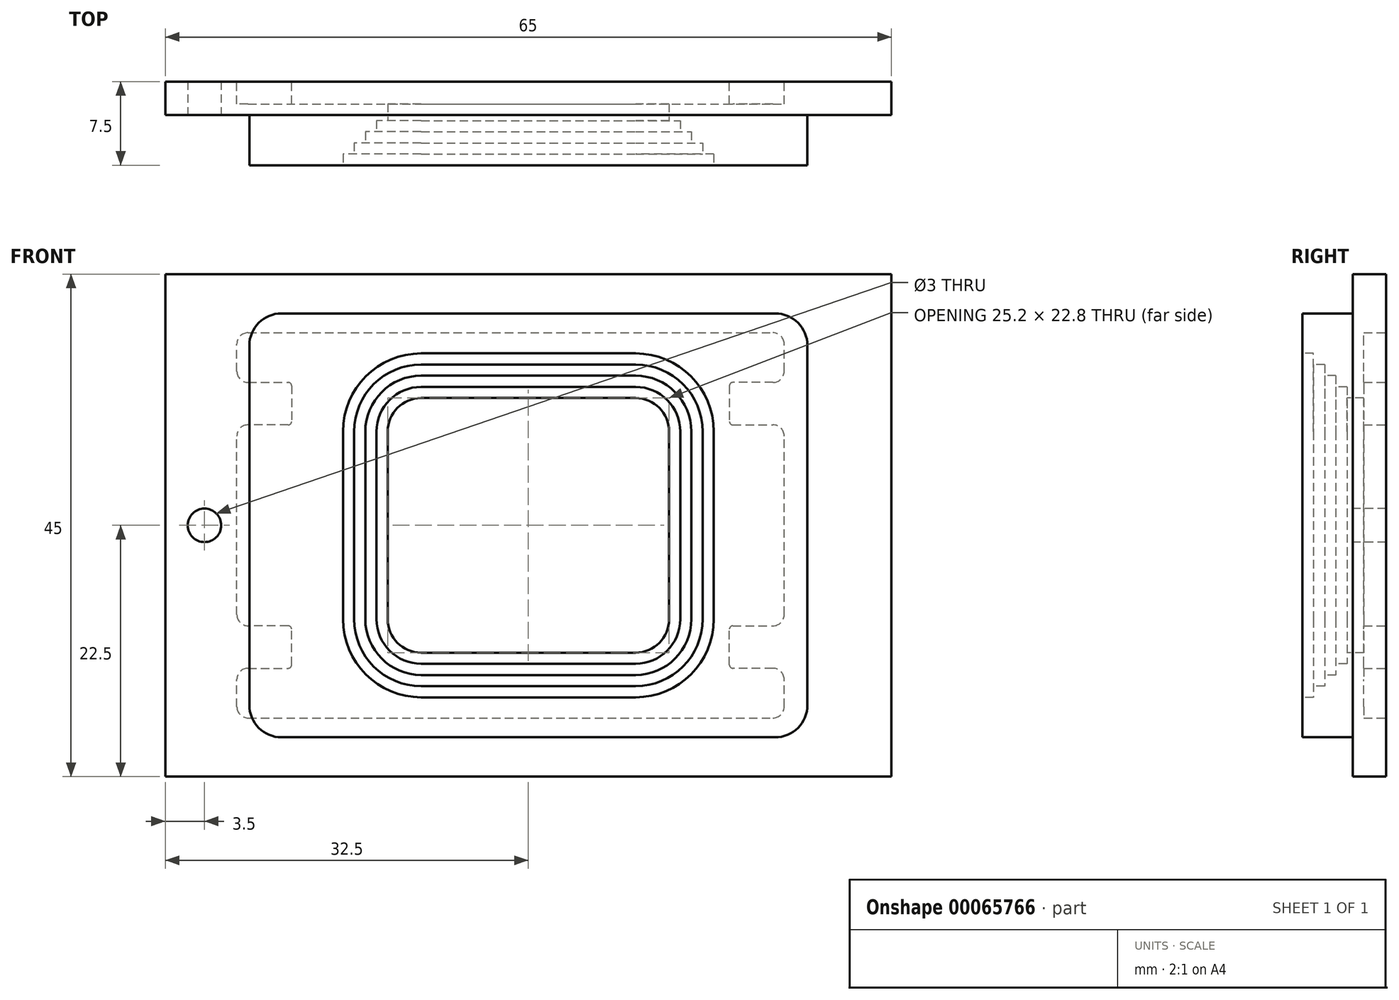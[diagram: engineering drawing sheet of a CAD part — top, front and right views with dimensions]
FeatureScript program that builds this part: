
annotation { "Feature Type Name" : "Feature", "Feature Type Description" : "" }
export const myFeature = defineFeature(function(context is Context, id is Id, definition is map)
    precondition{}
    {
        {
            var Q0;
            Q0=qCreatedBy(makeId("Front.planeOp"),FACE);
            var sketch = newSketch(context, id + "F0", { "sketchPlane" : qUnion([Q0])});
            skLineSegment(sketch, "E0.bottom", {"start": v(-32.5, 22.5) * mm, "end": v(32.5, 22.5) * mm});
            skLineSegment(sketch, "E0.top", {"start": v(-32.5, -22.5) * mm, "end": v(32.5, -22.5) * mm});
            skLineSegment(sketch, "E0.left", {"start": v(-32.5, 22.5) * mm, "end": v(-32.5, -22.5) * mm});
            skLineSegment(sketch, "E0.right", {"start": v(32.5, 22.5) * mm, "end": v(32.5, -22.5) * mm});
            skPoint(sketch, "E1.visualSharp", {"position": v(-32.5, 22.5) * mm});
            skLineSegment(sketch, "E1.filletArc", {"start": v(-32.5, 22.5) * mm, "end": v(-32.5, 22.5) * mm});
            skPoint(sketch, "E2.visualSharp", {"position": v(32.5, 22.5) * mm});
            skLineSegment(sketch, "E2.filletArc", {"start": v(32.5, 22.5) * mm, "end": v(32.5, 22.5) * mm});
            skPoint(sketch, "E3.visualSharp", {"position": v(32.5, -22.5) * mm});
            skLineSegment(sketch, "E3.filletArc", {"start": v(32.5, -22.5) * mm, "end": v(32.5, -22.5) * mm});
            skPoint(sketch, "E4.visualSharp", {"position": v(-32.5, -22.5) * mm});
            skLineSegment(sketch, "E4.filletArc", {"start": v(-32.5, -22.5) * mm, "end": v(-32.5, -22.5) * mm});
            skPoint(sketch, "E5", {"position": v(0, 22.5) * mm});
            skPoint(sketch, "E6", {"position": v(32.5, 0) * mm});
            skSolve(sketch);
        }
        {
            var Q0;
            Q0=makeQuery(id+"F0.imprint","IMPRINT",FACE,{"disambiguationData":[TD([[makeQuery(id+"F0.imprint","IMPRINT",EDGE,{"derivedFrom":sQuery(id+"F0.wireOp",EDGE,"E0.bottom")}),-1.0]])]});
            var Q1;
            Q1=makeQuery(id+"F0.imprint","IMPRINT",FACE,{"disambiguationData":[TD([[makeQuery(id+"F0.imprint","IMPRINT",EDGE,{"derivedFrom":sQuery(id+"F0.wireOp",EDGE,"E0.bottom")}),-1.0]])]});
            extrude(context, id + "F1", {"entities" : qUnion([Q0, Q1]), "depth" : 3 * mm});
        }
        {
            var Q0;
            Q0=makeQuery(id+"F1.opExtrude","CAP_FACE",FACE,{"disambiguationData":[OSD([sQuery(id+"F0.wireOp",EDGE,"E0.bottom"),sQuery(id+"F0.wireOp",EDGE,"E0.top"),sQuery(id+"F0.wireOp",EDGE,"E0.left"),sQuery(id+"F0.wireOp",EDGE,"E0.right"),sQuery(id+"F0.wireOp",EDGE,"E1.filletArc"),sQuery(id+"F0.wireOp",EDGE,"E2.filletArc"),sQuery(id+"F0.wireOp",EDGE,"E3.filletArc"),sQuery(id+"F0.wireOp",EDGE,"E4.filletArc")])],"isStart":false});
            var sketch = newSketch(context, id + "F2", { "sketchPlane" : qUnion([Q0])});
            skLineSegment(sketch, "E7.bottom", {"start": v(-22.09, 18.99) * mm, "end": v(22.09, 18.99) * mm});
            skLineSegment(sketch, "E7.top", {"start": v(-22.09, -18.99) * mm, "end": v(22.09, -18.99) * mm});
            skLineSegment(sketch, "E7.left", {"start": v(-24.98, 16.09) * mm, "end": v(-24.98, -16.09) * mm});
            skLineSegment(sketch, "E7.right", {"start": v(24.98, 16.09) * mm, "end": v(24.98, -16.09) * mm});
            skPoint(sketch, "E8", {"position": v(0, 18.99) * mm});
            skPoint(sketch, "E9", {"position": v(24.98, 0) * mm});
            skPoint(sketch, "E10.visualSharp", {"position": v(-24.98, 18.99) * mm});
            skArc(sketch, "E10.filletArc", {"start": v(-22.09, 18.99) * mm, "mid": v(-24.14, 18.14) * mm, "end": v(-24.98, 16.09) * mm});
            skPoint(sketch, "E11.visualSharp", {"position": v(24.99, -18.98) * mm});
            skArc(sketch, "E11.filletArc", {"start": v(22.09, -18.99) * mm, "mid": v(24.14, -18.14) * mm, "end": v(24.98, -16.09) * mm});
            skPoint(sketch, "E12.visualSharp", {"position": v(24.99, 18.98) * mm});
            skArc(sketch, "E12.filletArc", {"start": v(24.98, 16.09) * mm, "mid": v(24.14, 18.14) * mm, "end": v(22.09, 18.99) * mm});
            skPoint(sketch, "E13.visualSharp", {"position": v(-24.98, -18.99) * mm});
            skArc(sketch, "E13.filletArc", {"start": v(-24.98, -16.09) * mm, "mid": v(-24.14, -18.14) * mm, "end": v(-22.09, -18.99) * mm});
            skSolve(sketch);
        }
        {
            var Q0;
            Q0=makeQuery(id+"F2.imprint","IMPRINT",FACE,{"disambiguationData":[TD([[makeQuery(id+"F2.imprint","IMPRINT",EDGE,{"derivedFrom":sQuery(id+"F2.wireOp",EDGE,"E7.bottom")}),-1.0]])]});
            extrude(context, id + "F3", {"entities" : qUnion([Q0]), "operationType" : NewBodyOperationType.ADD, "depth" : 4.5 * mm});
        }
        {
            var Q0;
            Q0=makeQuery(id+"F3.opExtrude","CAP_FACE",FACE,{"disambiguationData":[OSD([sQuery(id+"F2.wireOp",EDGE,"E7.bottom"),sQuery(id+"F2.wireOp",EDGE,"E7.top"),sQuery(id+"F2.wireOp",EDGE,"E7.left"),sQuery(id+"F2.wireOp",EDGE,"E7.right"),sQuery(id+"F2.wireOp",EDGE,"E10.filletArc"),sQuery(id+"F2.wireOp",EDGE,"E11.filletArc"),sQuery(id+"F2.wireOp",EDGE,"E12.filletArc"),sQuery(id+"F2.wireOp",EDGE,"E13.filletArc")])],"isStart":false});
            var sketch = newSketch(context, id + "F4", { "sketchPlane" : qUnion([Q0])});
            skLineSegment(sketch, "E14.bottom", {"start": v(-9.6, 11.4) * mm, "end": v(9.6, 11.4) * mm});
            skLineSegment(sketch, "E14.top", {"start": v(-9.6, -11.4) * mm, "end": v(9.6, -11.4) * mm});
            skLineSegment(sketch, "E14.left", {"start": v(-12.6, 8.4) * mm, "end": v(-12.6, -8.4) * mm});
            skLineSegment(sketch, "E14.right", {"start": v(12.6, 8.4) * mm, "end": v(12.6, -8.4) * mm});
            skPoint(sketch, "E15", {"position": v(0, 11.4) * mm});
            skPoint(sketch, "E16", {"position": v(12.6, 0) * mm});
            skPoint(sketch, "E17.visualSharp", {"position": v(-12.6, 11.4) * mm});
            skArc(sketch, "E17.filletArc", {"start": v(-9.6, 11.4) * mm, "mid": v(-11.72, 10.52) * mm, "end": v(-12.6, 8.4) * mm});
            skPoint(sketch, "E18.visualSharp", {"position": v(12.6, 11.4) * mm});
            skArc(sketch, "E18.filletArc", {"start": v(12.6, 8.4) * mm, "mid": v(11.72, 10.52) * mm, "end": v(9.6, 11.4) * mm});
            skPoint(sketch, "E19.visualSharp", {"position": v(12.6, -11.4) * mm});
            skArc(sketch, "E19.filletArc", {"start": v(9.6, -11.4) * mm, "mid": v(11.72, -10.52) * mm, "end": v(12.6, -8.4) * mm});
            skPoint(sketch, "E20.visualSharp", {"position": v(-12.6, -11.4) * mm});
            skArc(sketch, "E20.filletArc", {"start": v(-12.6, -8.4) * mm, "mid": v(-11.72, -10.52) * mm, "end": v(-9.6, -11.4) * mm});
            skCircle(sketch, "E21", {"center": v(-29, 0) * mm, "radius": 1.5 * mm});
            skCircle(sketch, "E22.MirrorC", {"center": v(29, 0) * mm, "radius": 1.5 * mm});
            skSolve(sketch);
        }
        {
            var Q0;
            Q0=makeQuery(id+"F4.imprint","IMPRINT",FACE,{"disambiguationData":[TD([[makeQuery(id+"F4.imprint","IMPRINT",EDGE,{"derivedFrom":sQuery(id+"F4.wireOp",EDGE,"E14.bottom")}),-1.0]])]});
            var Q1;
            Q1=makeQuery(id+"F4.imprint","IMPRINT",FACE,{"disambiguationData":[TD([[makeQuery(id+"F4.imprint","IMPRINT",EDGE,{"derivedFrom":sQuery(id+"F4.wireOp",EDGE,"E21")}),1.0]])]});
            var Q2;
            Q2=makeQuery(id+"F4.imprint","IMPRINT",FACE,{"disambiguationData":[TD([[makeQuery(id+"F4.imprint","IMPRINT",EDGE,{"derivedFrom":sQuery(id+"F4.wireOp",EDGE,"E22.MirrorC")}),-1.0]])]});
            extrude(context, id + "F5", {"entities" : qUnion([Q0, Q1, Q2]), "operationType" : NewBodyOperationType.REMOVE, "oppositeDirection" : true, "depth" : 25 * mm});
        }
        {
            var Q0;
            Q0=makeQuery(id+"F1.opExtrude","CAP_FACE",FACE,{"disambiguationData":[OSD([sQuery(id+"F0.wireOp",EDGE,"E0.bottom"),sQuery(id+"F0.wireOp",EDGE,"E0.top"),sQuery(id+"F0.wireOp",EDGE,"E0.left"),sQuery(id+"F0.wireOp",EDGE,"E0.right")])],"isStart":true});
            var sketch = newSketch(context, id + "F6", { "sketchPlane" : qUnion([Q0])});
            skPoint(sketch, "E23", {"position": v(-32.5, 0) * mm});
            skPoint(sketch, "E23.positionSnap0", {"position": v(-22.9, 0) * mm});
            skLineSegment(sketch, "E24", {"start": v(-21.9, -12.8) * mm, "end": v(-18.3, -12.8) * mm});
            skLineSegment(sketch, "E25", {"start": v(-18, -12.5) * mm, "end": v(-18, -9.3) * mm});
            skLineSegment(sketch, "E26", {"start": v(-18.3, -9) * mm, "end": v(-21.9, -9) * mm});
            skLineSegment(sketch, "E27", {"start": v(-21.9, 12.8) * mm, "end": v(-18.3, 12.8) * mm});
            skLineSegment(sketch, "E28", {"start": v(-18, 12.5) * mm, "end": v(-18, 9.3) * mm});
            skLineSegment(sketch, "E29", {"start": v(-18.3, 9) * mm, "end": v(-21.9, 9) * mm});
            skLineSegment(sketch, "E30", {"start": v(1.6, 17.25) * mm, "end": v(1.6, -17.25) * mm, "construction": true});
            skLineSegment(sketch, "E31", {"start": v(-22.9, -16.25) * mm, "end": v(-22.9, -13.8) * mm});
            skLineSegment(sketch, "E32", {"start": v(-22.9, -8) * mm, "end": v(-22.9, 8) * mm});
            skLineSegment(sketch, "E33", {"start": v(-22.9, 13.8) * mm, "end": v(-22.9, 16.25) * mm});
            skPoint(sketch, "E34.visualSharp", {"position": v(-22.9, 12.8) * mm});
            skArc(sketch, "E34.filletArc", {"start": v(-22.9, 13.8) * mm, "mid": v(-22.6, 13.1) * mm, "end": v(-21.9, 12.8) * mm});
            skPoint(sketch, "E35.visualSharp", {"position": v(-22.9, 17.25) * mm});
            skArc(sketch, "E35.filletArc", {"start": v(-21.9, 17.25) * mm, "mid": v(-22.6, 16.96) * mm, "end": v(-22.9, 16.25) * mm});
            skPoint(sketch, "E36.visualSharp", {"position": v(-22.9, -9) * mm});
            skArc(sketch, "E36.filletArc", {"start": v(-22.9, -8) * mm, "mid": v(-22.6, -8.7) * mm, "end": v(-21.9, -9) * mm});
            skPoint(sketch, "E37.visualSharp", {"position": v(-22.9, -17.25) * mm});
            skArc(sketch, "E37.filletArc", {"start": v(-22.9, -16.25) * mm, "mid": v(-22.6, -16.96) * mm, "end": v(-21.9, -17.25) * mm});
            skPoint(sketch, "E38.visualSharp", {"position": v(-18, 9) * mm});
            skArc(sketch, "E38.filletArc", {"start": v(-18.3, 9) * mm, "mid": v(-18.09, 9.09) * mm, "end": v(-18, 9.3) * mm});
            skPoint(sketch, "E39.visualSharp", {"position": v(-18, 12.8) * mm});
            skArc(sketch, "E39.filletArc", {"start": v(-18, 12.5) * mm, "mid": v(-18.09, 12.71) * mm, "end": v(-18.3, 12.8) * mm});
            skPoint(sketch, "E40.visualSharp", {"position": v(-18, -9) * mm});
            skArc(sketch, "E40.filletArc", {"start": v(-18, -9.3) * mm, "mid": v(-18.09, -9.09) * mm, "end": v(-18.3, -9) * mm});
            skPoint(sketch, "E41.visualSharp", {"position": v(-18, -12.8) * mm});
            skArc(sketch, "E41.filletArc", {"start": v(-18.3, -12.8) * mm, "mid": v(-18.09, -12.71) * mm, "end": v(-18, -12.5) * mm});
            skPoint(sketch, "E42.visualSharp", {"position": v(-22.9, 9) * mm});
            skArc(sketch, "E42.filletArc", {"start": v(-21.9, 9) * mm, "mid": v(-22.6, 8.7) * mm, "end": v(-22.9, 8) * mm});
            skPoint(sketch, "E43.visualSharp", {"position": v(-22.9, -12.8) * mm});
            skArc(sketch, "E43.filletArc", {"start": v(-21.9, -12.8) * mm, "mid": v(-22.6, -13.1) * mm, "end": v(-22.9, -13.8) * mm});
            skArc(sketch, "E44.MirrorCS", {"start": v(26.1, -16.25) * mm, "mid": v(25.8, -16.96) * mm, "end": v(25.1, -17.25) * mm});
            skArc(sketch, "E45.MirrorCS", {"start": v(25.1, -12.8) * mm, "mid": v(25.8, -13.1) * mm, "end": v(26.1, -13.8) * mm});
            skLineSegment(sketch, "E46.MirrorCS", {"start": v(25.1, -12.8) * mm, "end": v(21.5, -12.8) * mm});
            skArc(sketch, "E47.MirrorCS", {"start": v(21.5, -12.8) * mm, "mid": v(21.29, -12.71) * mm, "end": v(21.2, -12.5) * mm});
            skLineSegment(sketch, "E48.MirrorCS", {"start": v(21.2, -12.5) * mm, "end": v(21.2, -9.3) * mm});
            skArc(sketch, "E49.MirrorCS", {"start": v(21.2, -9.3) * mm, "mid": v(21.29, -9.09) * mm, "end": v(21.5, -9) * mm});
            skLineSegment(sketch, "E50.MirrorCS", {"start": v(21.5, -9) * mm, "end": v(25.1, -9) * mm});
            skArc(sketch, "E51.MirrorCS", {"start": v(26.1, -8) * mm, "mid": v(25.8, -8.7) * mm, "end": v(25.1, -9) * mm});
            skLineSegment(sketch, "E52.MirrorCS", {"start": v(26.1, -8) * mm, "end": v(26.1, 8) * mm});
            skArc(sketch, "E53.MirrorCS", {"start": v(25.1, 9) * mm, "mid": v(25.8, 8.7) * mm, "end": v(26.1, 8) * mm});
            skLineSegment(sketch, "E54.MirrorCS", {"start": v(21.5, 9) * mm, "end": v(25.1, 9) * mm});
            skArc(sketch, "E55.MirrorCS", {"start": v(21.5, 9) * mm, "mid": v(21.29, 9.09) * mm, "end": v(21.2, 9.3) * mm});
            skLineSegment(sketch, "E56.MirrorCS", {"start": v(21.2, 12.5) * mm, "end": v(21.2, 9.3) * mm});
            skArc(sketch, "E57.MirrorCS", {"start": v(21.2, 12.5) * mm, "mid": v(21.29, 12.71) * mm, "end": v(21.5, 12.8) * mm});
            skLineSegment(sketch, "E58.MirrorCS", {"start": v(25.1, 12.8) * mm, "end": v(21.5, 12.8) * mm});
            skArc(sketch, "E59.MirrorCS", {"start": v(26.1, 13.8) * mm, "mid": v(25.8, 13.1) * mm, "end": v(25.1, 12.8) * mm});
            skLineSegment(sketch, "E60.MirrorCS", {"start": v(26.1, 13.8) * mm, "end": v(26.1, 16.25) * mm});
            skArc(sketch, "E61.MirrorCS", {"start": v(25.1, 17.25) * mm, "mid": v(25.8, 16.96) * mm, "end": v(26.1, 16.25) * mm});
            skLineSegment(sketch, "E62", {"start": v(25.1, -17.25) * mm, "end": v(-21.9, -17.25) * mm});
            skLineSegment(sketch, "E63", {"start": v(25.1, 17.25) * mm, "end": v(-21.9, 17.25) * mm});
            skLineSegment(sketch, "E64", {"start": v(-22.9, 0) * mm, "end": v(26.1, 0) * mm, "construction": true});
            skLineSegment(sketch, "E65.MirrorCS", {"start": v(26.1, -16.25) * mm, "end": v(26.1, -13.8) * mm});
            skSolve(sketch);
        }
        {
            var Q0;
            Q0=makeQuery(id+"F6.imprint","IMPRINT",FACE,{"disambiguationData":[TD([[makeQuery(id+"F6.imprint","IMPRINT",EDGE,{"derivedFrom":sQuery(id+"F6.wireOp",EDGE,"E24")}),-1.0]])]});
            extrude(context, id + "F7", {"entities" : qUnion([Q0]), "operationType" : NewBodyOperationType.REMOVE, "oppositeDirection" : true, "depth" : 2 * mm});
        }
        {
            var Q0;
            Q0=makeQuery(id+"F3.opExtrude","CAP_FACE",FACE,{"disambiguationData":[OSD([sQuery(id+"F2.wireOp",EDGE,"E7.bottom"),sQuery(id+"F2.wireOp",EDGE,"E7.top"),sQuery(id+"F2.wireOp",EDGE,"E7.left"),sQuery(id+"F2.wireOp",EDGE,"E7.right"),sQuery(id+"F2.wireOp",EDGE,"E10.filletArc"),sQuery(id+"F2.wireOp",EDGE,"E11.filletArc"),sQuery(id+"F2.wireOp",EDGE,"E12.filletArc"),sQuery(id+"F2.wireOp",EDGE,"E13.filletArc")])],"isStart":false});
            var sketch = newSketch(context, id + "F8", { "sketchPlane" : qUnion([Q0])});
            skLineSegment(sketch, "E66.0", {"start": v(-9.6, 12.4) * mm, "end": v(9.6, 12.4) * mm});
            skArc(sketch, "E66.1", {"start": v(13.6, 8.4) * mm, "mid": v(12.43, 11.23) * mm, "end": v(9.6, 12.4) * mm});
            skArc(sketch, "E66.2", {"start": v(-9.6, 12.4) * mm, "mid": v(-12.43, 11.23) * mm, "end": v(-13.6, 8.4) * mm});
            skLineSegment(sketch, "E66.3", {"start": v(13.6, 8.4) * mm, "end": v(13.6, -8.4) * mm});
            skLineSegment(sketch, "E66.4", {"start": v(-13.6, 8.4) * mm, "end": v(-13.6, -8.4) * mm});
            skArc(sketch, "E66.5", {"start": v(-13.6, -8.4) * mm, "mid": v(-12.43, -11.23) * mm, "end": v(-9.6, -12.4) * mm});
            skLineSegment(sketch, "E66.6", {"start": v(-9.6, -12.4) * mm, "end": v(9.6, -12.4) * mm});
            skArc(sketch, "E66.7", {"start": v(9.6, -12.4) * mm, "mid": v(12.43, -11.23) * mm, "end": v(13.6, -8.4) * mm});
            skSolve(sketch);
        }
        {
            var Q0;
            Q0=makeQuery(id+"F8.imprint","IMPRINT",FACE,{"disambiguationData":[TD([[makeQuery(id+"F8.imprint","IMPRINT",EDGE,{"derivedFrom":sQuery(id+"F8.wireOp",EDGE,"E66.0")}),-1.0]])]});
            extrude(context, id + "F9", {"entities" : qUnion([Q0]), "operationType" : NewBodyOperationType.REMOVE, "oppositeDirection" : true, "depth" : 4 * mm});
        }
        {
            var Q0;
            Q0=makeQuery(id+"F3.opExtrude","CAP_FACE",FACE,{"disambiguationData":[OSD([sQuery(id+"F2.wireOp",EDGE,"E7.bottom"),sQuery(id+"F2.wireOp",EDGE,"E7.top"),sQuery(id+"F2.wireOp",EDGE,"E7.left"),sQuery(id+"F2.wireOp",EDGE,"E7.right"),sQuery(id+"F2.wireOp",EDGE,"E10.filletArc"),sQuery(id+"F2.wireOp",EDGE,"E11.filletArc"),sQuery(id+"F2.wireOp",EDGE,"E12.filletArc"),sQuery(id+"F2.wireOp",EDGE,"E13.filletArc")])],"isStart":false});
            var sketch = newSketch(context, id + "F10", { "sketchPlane" : qUnion([Q0])});
            skLineSegment(sketch, "E67.0", {"start": v(-9.6, 13.4) * mm, "end": v(9.6, 13.4) * mm});
            skArc(sketch, "E67.1", {"start": v(14.6, 8.4) * mm, "mid": v(13.14, 11.94) * mm, "end": v(9.6, 13.4) * mm});
            skArc(sketch, "E67.2", {"start": v(-9.6, 13.4) * mm, "mid": v(-13.14, 11.94) * mm, "end": v(-14.6, 8.4) * mm});
            skLineSegment(sketch, "E67.3", {"start": v(14.6, 8.4) * mm, "end": v(14.6, -8.4) * mm});
            skLineSegment(sketch, "E67.4", {"start": v(-14.6, 8.4) * mm, "end": v(-14.6, -8.4) * mm});
            skArc(sketch, "E67.5", {"start": v(-14.6, -8.4) * mm, "mid": v(-13.14, -11.94) * mm, "end": v(-9.6, -13.4) * mm});
            skLineSegment(sketch, "E67.6", {"start": v(-9.6, -13.4) * mm, "end": v(9.6, -13.4) * mm});
            skArc(sketch, "E67.7", {"start": v(9.6, -13.4) * mm, "mid": v(13.14, -11.94) * mm, "end": v(14.6, -8.4) * mm});
            skLineSegment(sketch, "E68.0", {"start": v(19.98, 13.99) * mm, "end": v(-19.98, 13.99) * mm});
            skLineSegment(sketch, "E68.1", {"start": v(19.98, -13.99) * mm, "end": v(19.98, 13.99) * mm});
            skLineSegment(sketch, "E68.2", {"start": v(-19.98, -13.99) * mm, "end": v(19.98, -13.99) * mm});
            skLineSegment(sketch, "E68.3", {"start": v(-19.98, 13.99) * mm, "end": v(-19.98, -13.99) * mm});
            skSolve(sketch);
        }
        {
            var Q0;
            Q0=makeQuery(id+"F10.imprint","IMPRINT",FACE,{"disambiguationData":[TD([[makeQuery(id+"F10.imprint","IMPRINT",EDGE,{"derivedFrom":sQuery(id+"F10.wireOp",EDGE,"E67.0")}),-1.0]])]});
            extrude(context, id + "F11", {"entities" : qUnion([Q0]), "operationType" : NewBodyOperationType.REMOVE, "oppositeDirection" : true, "depth" : 3 * mm});
        }
        {
            var Q0;
            Q0=makeQuery(id+"F3.opExtrude","CAP_FACE",FACE,{"disambiguationData":[OSD([sQuery(id+"F2.wireOp",EDGE,"E7.bottom"),sQuery(id+"F2.wireOp",EDGE,"E7.top"),sQuery(id+"F2.wireOp",EDGE,"E7.left"),sQuery(id+"F2.wireOp",EDGE,"E7.right"),sQuery(id+"F2.wireOp",EDGE,"E10.filletArc"),sQuery(id+"F2.wireOp",EDGE,"E11.filletArc"),sQuery(id+"F2.wireOp",EDGE,"E12.filletArc"),sQuery(id+"F2.wireOp",EDGE,"E13.filletArc")])],"isStart":false});
            var sketch = newSketch(context, id + "F12", { "sketchPlane" : qUnion([Q0])});
            skLineSegment(sketch, "E69.0", {"start": v(-9.6, 14.4) * mm, "end": v(9.6, 14.4) * mm});
            skArc(sketch, "E69.1", {"start": v(15.6, 8.4) * mm, "mid": v(13.84, 12.64) * mm, "end": v(9.6, 14.4) * mm});
            skArc(sketch, "E69.2", {"start": v(-9.6, 14.4) * mm, "mid": v(-13.84, 12.64) * mm, "end": v(-15.6, 8.4) * mm});
            skLineSegment(sketch, "E69.3", {"start": v(15.6, 8.4) * mm, "end": v(15.6, -8.4) * mm});
            skLineSegment(sketch, "E69.4", {"start": v(-15.6, 8.4) * mm, "end": v(-15.6, -8.4) * mm});
            skArc(sketch, "E69.5", {"start": v(-15.6, -8.4) * mm, "mid": v(-13.84, -12.64) * mm, "end": v(-9.6, -14.4) * mm});
            skLineSegment(sketch, "E69.6", {"start": v(-9.6, -14.4) * mm, "end": v(9.6, -14.4) * mm});
            skArc(sketch, "E69.7", {"start": v(9.6, -14.4) * mm, "mid": v(13.84, -12.64) * mm, "end": v(15.6, -8.4) * mm});
            skSolve(sketch);
        }
        {
            var Q0;
            Q0=makeQuery(id+"F12.imprint","IMPRINT",FACE,{"disambiguationData":[TD([[makeQuery(id+"F12.imprint","IMPRINT",EDGE,{"derivedFrom":sQuery(id+"F12.wireOp",EDGE,"E69.0")}),-1.0]])]});
            extrude(context, id + "F13", {"entities" : qUnion([Q0]), "operationType" : NewBodyOperationType.REMOVE, "oppositeDirection" : true, "depth" : 2 * mm});
        }
        {
            var Q0;
            Q0=makeQuery(id+"F3.opExtrude","CAP_FACE",FACE,{"disambiguationData":[OSD([sQuery(id+"F2.wireOp",EDGE,"E7.bottom"),sQuery(id+"F2.wireOp",EDGE,"E7.top"),sQuery(id+"F2.wireOp",EDGE,"E7.left"),sQuery(id+"F2.wireOp",EDGE,"E7.right"),sQuery(id+"F2.wireOp",EDGE,"E10.filletArc"),sQuery(id+"F2.wireOp",EDGE,"E11.filletArc"),sQuery(id+"F2.wireOp",EDGE,"E12.filletArc"),sQuery(id+"F2.wireOp",EDGE,"E13.filletArc")])],"isStart":false});
            var sketch = newSketch(context, id + "F14", { "sketchPlane" : qUnion([Q0])});
            skLineSegment(sketch, "E70.0", {"start": v(-9.6, 15.4) * mm, "end": v(9.6, 15.4) * mm});
            skArc(sketch, "E70.1", {"start": v(16.6, 8.4) * mm, "mid": v(14.55, 13.35) * mm, "end": v(9.6, 15.4) * mm});
            skArc(sketch, "E70.2", {"start": v(-9.6, 15.4) * mm, "mid": v(-14.55, 13.35) * mm, "end": v(-16.6, 8.4) * mm});
            skLineSegment(sketch, "E70.3", {"start": v(16.6, 8.4) * mm, "end": v(16.6, -8.4) * mm});
            skLineSegment(sketch, "E70.4", {"start": v(-16.6, 8.4) * mm, "end": v(-16.6, -8.4) * mm});
            skArc(sketch, "E70.5", {"start": v(-16.6, -8.4) * mm, "mid": v(-14.55, -13.35) * mm, "end": v(-9.6, -15.4) * mm});
            skLineSegment(sketch, "E70.6", {"start": v(-9.6, -15.4) * mm, "end": v(9.6, -15.4) * mm});
            skArc(sketch, "E70.7", {"start": v(9.6, -15.4) * mm, "mid": v(14.55, -13.35) * mm, "end": v(16.6, -8.4) * mm});
            skLineSegment(sketch, "E71.0", {"start": v(19.98, 13.99) * mm, "end": v(-19.98, 13.99) * mm});
            skLineSegment(sketch, "E71.1", {"start": v(19.98, -13.99) * mm, "end": v(19.98, 13.99) * mm});
            skLineSegment(sketch, "E71.2", {"start": v(-19.98, -13.99) * mm, "end": v(19.98, -13.99) * mm});
            skLineSegment(sketch, "E71.3", {"start": v(-19.98, 13.99) * mm, "end": v(-19.98, -13.99) * mm});
            skSolve(sketch);
        }
        {
            var Q0;
            {var subQ5=makeQuery(id+"F13.boolean.opBoolean","COPY",EDGE,{"derivedFrom":makeQuery(id+"F13.opExtrude","CAP_EDGE",EDGE,{"disambiguationData":[OSD([sQuery(id+"F12.wireOp",EDGE,"E69.0")])],"isStart":true})});Q0=makeQuery(id+"F14.imprint","IMPRINT",FACE,{"disambiguationData":[TD([[makeQuery(id+"F14.imprint","IMPRINT",EDGE,{"derivedFrom":subQ5}),-1.0]])]});}
            var Q1;
            {var subQ5=makeQuery(id+"F13.boolean.opBoolean","COPY",EDGE,{"derivedFrom":makeQuery(id+"F13.opExtrude","CAP_EDGE",EDGE,{"disambiguationData":[OSD([sQuery(id+"F12.wireOp",EDGE,"E69.6")])],"isStart":true})});Q1=makeQuery(id+"F14.imprint","IMPRINT",FACE,{"disambiguationData":[TD([[makeQuery(id+"F14.imprint","IMPRINT",EDGE,{"derivedFrom":subQ5}),1.0]])]});}
            var Q2;
            {var subQ6=sQuery(id+"F14.wireOp",EDGE,"E70.0");Q2=makeQuery(id+"F14.imprint","IMPRINT",FACE,{"disambiguationData":[TD([[makeQuery(id+"F14.imprint","IMPRINT",EDGE,{"derivedFrom":subQ6}),-1.0]])]});}
            var Q3;
            {var subQ9=sQuery(id+"F14.wireOp",EDGE,"E70.3");Q3=makeQuery(id+"F14.imprint","IMPRINT",FACE,{"disambiguationData":[TD([[makeQuery(id+"F14.imprint","IMPRINT",EDGE,{"derivedFrom":subQ9}),-1.0]])]});}
            var Q4;
            {var subQ6=sQuery(id+"F14.wireOp",EDGE,"E70.4");Q4=makeQuery(id+"F14.imprint","IMPRINT",FACE,{"disambiguationData":[TD([[makeQuery(id+"F14.imprint","IMPRINT",EDGE,{"derivedFrom":subQ6}),1.0]])]});}
            var Q5;
            {var subQ6=sQuery(id+"F14.wireOp",EDGE,"E70.6");Q5=makeQuery(id+"F14.imprint","IMPRINT",FACE,{"disambiguationData":[TD([[makeQuery(id+"F14.imprint","IMPRINT",EDGE,{"derivedFrom":subQ6}),1.0]])]});}
            var Q6;
            {var subQ0=makeQuery(id+"F13.boolean.opBoolean","COPY",EDGE,{"derivedFrom":makeQuery(id+"F13.opExtrude","CAP_EDGE",EDGE,{"disambiguationData":[OSD([sQuery(id+"F12.wireOp",EDGE,"E69.3")])],"isStart":true})});Q6=makeQuery(id+"F14.imprint","IMPRINT",FACE,{"disambiguationData":[TD([[makeQuery(id+"F14.imprint","IMPRINT",EDGE,{"derivedFrom":subQ0}),-1.0]])]});}
            extrude(context, id + "F15", {"entities" : qUnion([Q0, Q1, Q2, Q3, Q4, Q5, Q6]), "operationType" : NewBodyOperationType.REMOVE, "oppositeDirection" : true, "depth" : 1 * mm});
        }
    });
